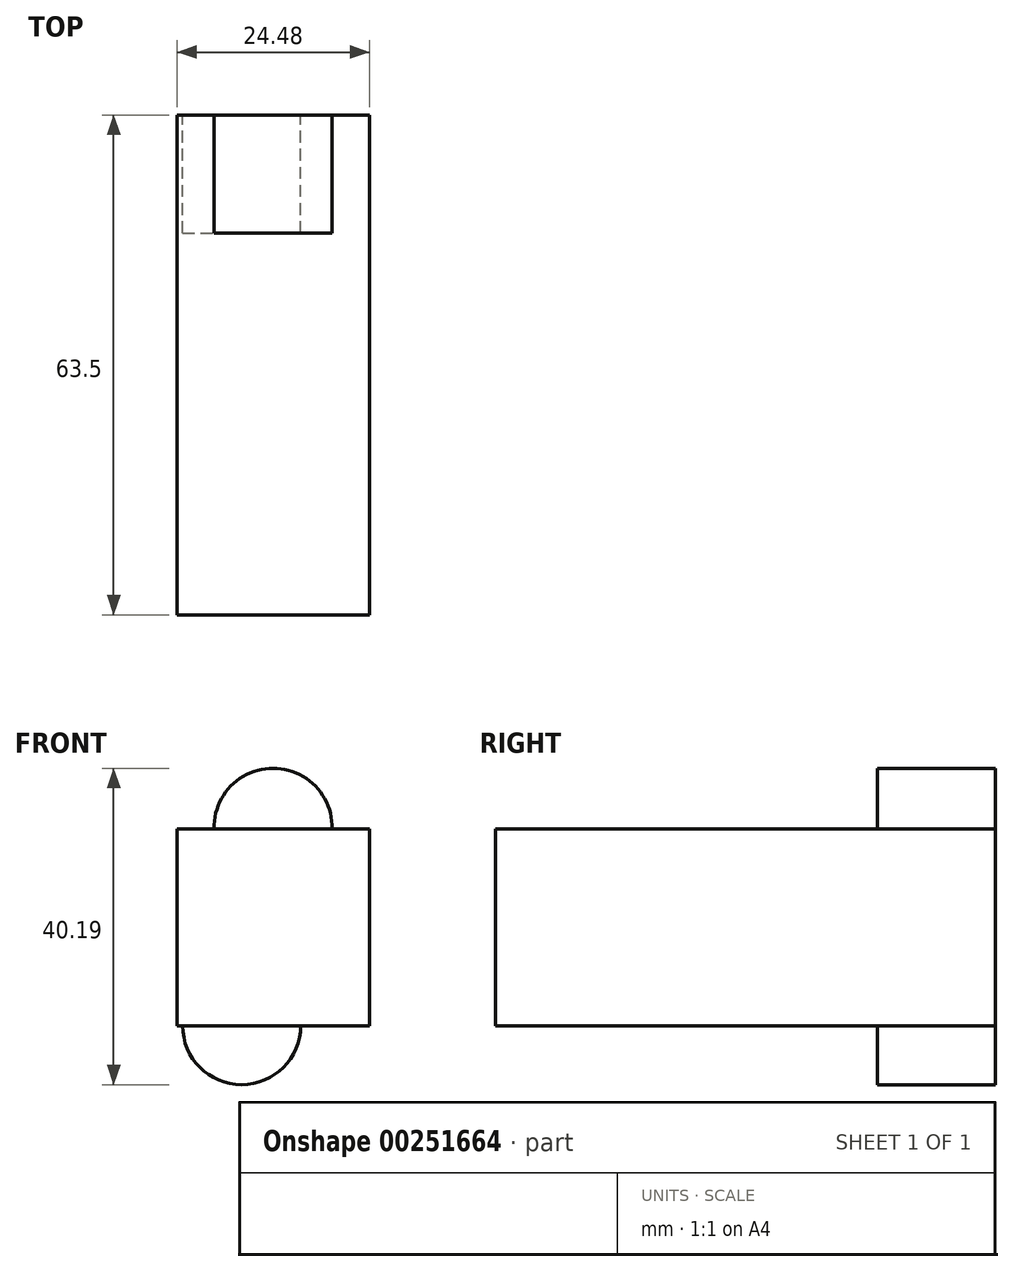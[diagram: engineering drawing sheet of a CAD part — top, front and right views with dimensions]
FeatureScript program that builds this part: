
annotation { "Feature Type Name" : "Feature", "Feature Type Description" : "" }
export const myFeature = defineFeature(function(context is Context, id is Id, definition is map)
    precondition{}
    {
        {
            var Q0;
            Q0=qCreatedBy(makeId("Front.planeOp"),FACE);
            var sketch = newSketch(context, id + "F0", { "sketchPlane" : qUnion([Q0])});
            skLineSegment(sketch, "E0.bottom", {"start": v(0, 0) * mm, "end": v(24.48, 0) * mm});
            skLineSegment(sketch, "E0.top", {"start": v(0, 25) * mm, "end": v(24.48, 25) * mm});
            skLineSegment(sketch, "E0.left", {"start": v(0, 0) * mm, "end": v(0, 25) * mm});
            skLineSegment(sketch, "E0.right", {"start": v(24.48, 0) * mm, "end": v(24.48, 25) * mm});
            skSolve(sketch);
        }
        {
            var Q0;
            Q0 = qSketchRegion(id + "F0", true);
            extrude(context, id + "F1", {"entities" : qUnion([Q0]), "depth" : 63.5 * mm});
        }
        {
            var Q0;
            Q0=qCreatedBy(makeId("Front.planeOp"),FACE);
            var sketch = newSketch(context, id + "F2", { "sketchPlane" : qUnion([Q0])});
            skCircle(sketch, "E1", {"center": v(12.23, 25.2) * mm, "radius": 7.5 * mm});
            skSolve(sketch);
        }
        {
            var Q0;
            Q0 = qSketchRegion(id + "F2", true);
            extrude(context, id + "F3", {"entities" : qUnion([Q0]), "operationType" : NewBodyOperationType.ADD, "depth" : 15 * mm});
        }
        {
            var Q0;
            Q0=qCreatedBy(makeId("Front.planeOp"),FACE);
            var sketch = newSketch(context, id + "F4", { "sketchPlane" : qUnion([Q0])});
            skCircle(sketch, "E2", {"center": v(8.24, 0) * mm, "radius": 7.5 * mm});
            skSolve(sketch);
        }
        {
            var Q0;
            Q0 = qSketchRegion(id + "F4", true);
            extrude(context, id + "F5", {"entities" : qUnion([Q0]), "operationType" : NewBodyOperationType.ADD, "depth" : 15 * mm});
        }
    });
